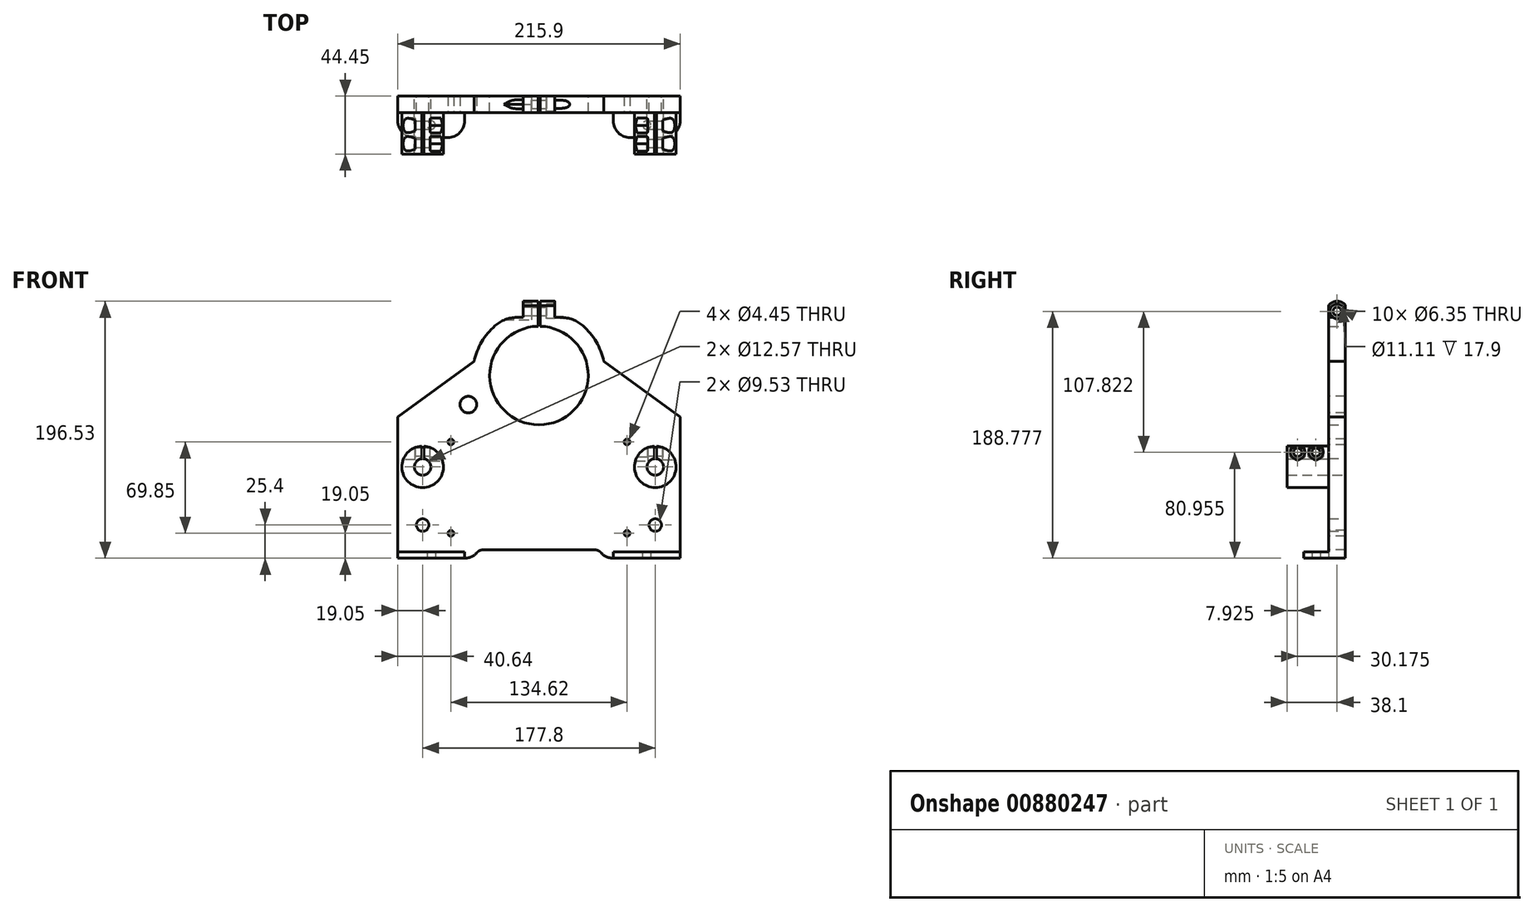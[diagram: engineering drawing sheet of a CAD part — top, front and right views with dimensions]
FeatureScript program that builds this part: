
annotation { "Feature Type Name" : "Feature", "Feature Type Description" : "" }
export const myFeature = defineFeature(function(context is Context, id is Id, definition is map)
    precondition{}
    {
        {
            var Q0;
            Q0=qCreatedBy(makeId("Front.planeOp"),FACE);
            var sketch = newSketch(context, id + "F0", { "sketchPlane" : qUnion([Q0])});
            skCircle(sketch, "E0", {"center": v(-88.9, 0) * mm, "radius": 6.29 * mm});
            skCircle(sketch, "E1", {"center": v(88.9, 0) * mm, "radius": 6.29 * mm});
            skCircle(sketch, "E2", {"center": v(-88.9, -44.45) * mm, "radius": 4.76 * mm});
            skCircle(sketch, "E3", {"center": v(88.9, -44.45) * mm, "radius": 4.76 * mm});
            skLineSegment(sketch, "E4.top", {"start": v(-107.95, -69.85) * mm, "end": v(107.95, -69.85) * mm});
            skLineSegment(sketch, "E4.left", {"start": v(-107.95, 38.1) * mm, "end": v(-107.95, -69.85) * mm});
            skLineSegment(sketch, "E4.right", {"start": v(107.95, 38.1) * mm, "end": v(107.95, -69.85) * mm});
            skPoint(sketch, "E4.middle", {"position": v(0, -15.87) * mm});
            skCircle(sketch, "E5", {"center": v(0, 69.85) * mm, "radius": 37.66 * mm});
            skArc(sketch, "E6", {"start": v(22.5, 100.6) * mm, "mid": v(0, 107.95) * mm, "end": v(-22.5, 100.6) * mm});
            skLineSegment(sketch, "E7", {"start": v(-107.95, 38.1) * mm, "end": v(-22.5, 100.6) * mm});
            skLineSegment(sketch, "E8", {"start": v(107.95, 38.1) * mm, "end": v(22.5, 100.6) * mm});
            skPoint(sketch, "E9.center.orphan", {"position": v(0, 0) * mm});
            skSolve(sketch);
        }
        {
            var Q0;
            Q0=qSketchRegion(id+"F0",true);
            extrude(context, id + "F1", {"entities" : qUnion([Q0]), "depth" : 12.7 * mm});
        }
        {
            var Q0;
            Q0=makeQuery(id+"F1.opExtrude","CAP_FACE",FACE,{"disambiguationData":[OSD([sQuery(id+"F0.wireOp",EDGE,"E9"),sQuery(id+"F0.wireOp",EDGE,"E0"),sQuery(id+"F0.wireOp",EDGE,"E1"),sQuery(id+"F0.wireOp",EDGE,"E2"),sQuery(id+"F0.wireOp",EDGE,"E3"),sQuery(id+"F0.wireOp",EDGE,"E4.bottom"),sQuery(id+"F0.wireOp",EDGE,"E4.top"),sQuery(id+"F0.wireOp",EDGE,"E4.left"),sQuery(id+"F0.wireOp",EDGE,"E4.right")])],"isStart":false});
            var sketch = newSketch(context, id + "F2", { "sketchPlane" : qUnion([Q0])});
            skCircle(sketch, "E10", {"center": v(0, -107.95) * mm, "radius": 63.5 * mm});
            skSolve(sketch);
        }
        {
            var Q0;
            Q0=qSketchRegion(id+"F2",true);
            extrude(context, id + "F3", {"entities" : qUnion([Q0]), "operationType" : NewBodyOperationType.REMOVE, "oppositeDirection" : true, "depth" : 25.4 * mm});
        }
        {
            var Q0;
            Q0=makeQuery(id+"F3.boolean.opBoolean","INTERSECT",EDGE,{"disambiguationData":[OD(0.0)],"derivedFrom":[makeQuery(id+"F1.opExtrude","SWEPT_FACE",FACE,{"disambiguationData":[OSD([sQuery(id+"F0.wireOp",EDGE,"E4.top")])]}),makeQuery(id+"F3.opExtrude","SWEPT_FACE",FACE,{"disambiguationData":[OSD([sQuery(id+"F2.wireOp",EDGE,"E10")])]})]});
            var Q1;
            Q1=makeQuery(id+"F3.boolean.opBoolean","INTERSECT",EDGE,{"disambiguationData":[OD(1.0)],"derivedFrom":[makeQuery(id+"F1.opExtrude","SWEPT_FACE",FACE,{"disambiguationData":[OSD([sQuery(id+"F0.wireOp",EDGE,"E4.top")])]}),makeQuery(id+"F3.opExtrude","SWEPT_FACE",FACE,{"disambiguationData":[OSD([sQuery(id+"F2.wireOp",EDGE,"E10")])]})]});
            fillet(context, id + "F4", {"entities" : qUnion([Q0, Q1]), "radius" : 12.7 * mm, "tangentPropagation" : true, "allowEdgeOverflow" : false});
        }
        {
            var Q0;
            Q0=makeQuery(id+"F1.opExtrude","CAP_FACE",FACE,{"disambiguationData":[OSD([sQuery(id+"F0.wireOp",EDGE,"E9"),sQuery(id+"F0.wireOp",EDGE,"E0"),sQuery(id+"F0.wireOp",EDGE,"E1"),sQuery(id+"F0.wireOp",EDGE,"E2"),sQuery(id+"F0.wireOp",EDGE,"E3"),sQuery(id+"F0.wireOp",EDGE,"E4.bottom"),sQuery(id+"F0.wireOp",EDGE,"E4.top"),sQuery(id+"F0.wireOp",EDGE,"E4.left"),sQuery(id+"F0.wireOp",EDGE,"E4.right")])],"isStart":false});
            var sketch = newSketch(context, id + "F5", { "sketchPlane" : qUnion([Q0])});
            skCircle(sketch, "E11.0", {"center": v(-88.9, 0) * mm, "radius": 6.29 * mm});
            skCircle(sketch, "E12", {"center": v(-88.9, 0) * mm, "radius": 15.88 * mm});
            skCircle(sketch, "E13.0", {"center": v(88.9, 0) * mm, "radius": 6.29 * mm});
            skCircle(sketch, "E14", {"center": v(88.9, 0) * mm, "radius": 15.88 * mm});
            skSolve(sketch);
        }
        {
            var Q0;
            Q0=qSketchRegion(id+"F5",true);
            extrude(context, id + "F6", {"entities" : qUnion([Q0]), "operationType" : NewBodyOperationType.ADD, "depth" : 31.75 * mm});
        }
        {
            var Q0;
            Q0=makeQuery(id+"F6.opExtrude","CAP_FACE",FACE,{"disambiguationData":[OSD([sQuery(id+"F5.wireOp",EDGE,"E11.0"),sQuery(id+"F5.wireOp",EDGE,"E12")])],"isStart":false});
            var sketch = newSketch(context, id + "F7", { "sketchPlane" : qUnion([Q0])});
            skLineSegment(sketch, "E15.bottom", {"start": v(-89.7, 1.72) * mm, "end": v(-88.1, 1.72) * mm});
            skLineSegment(sketch, "E15.top", {"start": v(-89.7, 19.66) * mm, "end": v(-88.1, 19.66) * mm});
            skLineSegment(sketch, "E15.left", {"start": v(-89.7, 1.72) * mm, "end": v(-89.7, 19.66) * mm});
            skLineSegment(sketch, "E15.right", {"start": v(-88.1, 1.72) * mm, "end": v(-88.1, 19.66) * mm});
            skLineSegment(sketch, "E16", {"start": v(-88.9, 1.72) * mm, "end": v(-88.9, 0) * mm});
            skPoint(sketch, "E16.endSnap0", {"position": v(-88.9, 1.72) * mm});
            skLineSegment(sketch, "E17.bottom", {"start": v(88.1, 20.83) * mm, "end": v(89.7, 20.83) * mm});
            skLineSegment(sketch, "E17.top", {"start": v(88.1, 3.08) * mm, "end": v(89.7, 3.08) * mm});
            skLineSegment(sketch, "E17.left", {"start": v(88.1, 20.83) * mm, "end": v(88.1, 3.08) * mm});
            skLineSegment(sketch, "E17.right", {"start": v(89.7, 20.83) * mm, "end": v(89.7, 3.08) * mm});
            skLineSegment(sketch, "E18", {"start": v(88.9, 0) * mm, "end": v(88.9, 3.08) * mm});
            skSolve(sketch);
        }
        {
            var Q0;
            Q0=qSketchRegion(id+"F7",true);
            var Q1;
            Q1=makeQuery(id+"F1.opExtrude","CAP_FACE",FACE,{"disambiguationData":[OSD([sQuery(id+"F0.wireOp",EDGE,"E9"),sQuery(id+"F0.wireOp",EDGE,"E0"),sQuery(id+"F0.wireOp",EDGE,"E1"),sQuery(id+"F0.wireOp",EDGE,"E2"),sQuery(id+"F0.wireOp",EDGE,"E3"),sQuery(id+"F0.wireOp",EDGE,"E4.bottom"),sQuery(id+"F0.wireOp",EDGE,"E4.top"),sQuery(id+"F0.wireOp",EDGE,"E4.left"),sQuery(id+"F0.wireOp",EDGE,"E4.right")])],"isStart":false});
            extrude(context, id + "F8", {"entities" : qUnion([Q0]), "operationType" : NewBodyOperationType.REMOVE, "endBound" : BoundingType.UP_TO_SURFACE, "oppositeDirection" : true, "endBoundEntityFace" : qUnion([Q1]), "depth" : 25.4 * mm});
        }
        {
            var Q0;
            Q0=makeQuery(id+"F1.opExtrude","SWEPT_FACE",FACE,{"disambiguationData":[OSD([sQuery(id+"F0.wireOp",EDGE,"E4.left")])]});
            var sketch = newSketch(context, id + "F9", { "sketchPlane" : qUnion([Q0])});
            skCircle(sketch, "E19", {"center": v(36.53, 11.1) * mm, "radius": 3.18 * mm});
            skCircle(sketch, "E20", {"center": v(22.56, 11.1) * mm, "radius": 3.18 * mm});
            skSolve(sketch);
        }
        {
            var Q0;
            Q0=qSketchRegion(id+"F9",true);
            extrude(context, id + "F10", {"entities" : qUnion([Q0]), "operationType" : NewBodyOperationType.REMOVE, "oppositeDirection" : true, "depth" : 224.54 * mm});
        }
        {
            var Q0;
            Q0=qCreatedBy(makeId("Right.planeOp"),FACE);
            var sketch = newSketch(context, id + "F11", { "sketchPlane" : qUnion([Q0])});
            skCircle(sketch, "E21.0", {"center": v(-36.53, 11.1) * mm, "radius": 3.17 * mm, "construction": true});
            skCircle(sketch, "E22.0", {"center": v(-22.56, 11.1) * mm, "radius": 3.18 * mm, "construction": true});
            skCircle(sketch, "E23.cCircle", {"center": v(-36.53, 11.1) * mm, "radius": 6.6 * mm, "construction": true});
            skLineSegment(sketch, "E23.0", {"start": v(-36.53, 17.7) * mm, "end": v(-30.8, 14.4) * mm});
            skLineSegment(sketch, "E23.1", {"start": v(-30.8, 14.4) * mm, "end": v(-30.8, 7.8) * mm});
            skLineSegment(sketch, "E23.2", {"start": v(-30.8, 7.8) * mm, "end": v(-36.53, 4.5) * mm});
            skLineSegment(sketch, "E23.3", {"start": v(-36.53, 4.5) * mm, "end": v(-42.24, 7.8) * mm});
            skLineSegment(sketch, "E23.4", {"start": v(-42.24, 7.8) * mm, "end": v(-42.24, 14.4) * mm});
            skLineSegment(sketch, "E23.5", {"start": v(-42.24, 14.4) * mm, "end": v(-36.53, 17.7) * mm});
            skCircle(sketch, "E24.cCircle", {"center": v(-22.56, 11.1) * mm, "radius": 6.6 * mm, "construction": true});
            skLineSegment(sketch, "E24.0", {"start": v(-28.27, 14.4) * mm, "end": v(-22.56, 17.7) * mm});
            skLineSegment(sketch, "E24.1", {"start": v(-22.56, 17.7) * mm, "end": v(-16.84, 14.4) * mm});
            skLineSegment(sketch, "E24.2", {"start": v(-16.84, 14.4) * mm, "end": v(-16.84, 7.8) * mm});
            skLineSegment(sketch, "E24.3", {"start": v(-16.84, 7.8) * mm, "end": v(-22.56, 4.5) * mm});
            skLineSegment(sketch, "E24.4", {"start": v(-22.56, 4.5) * mm, "end": v(-28.27, 7.8) * mm});
            skLineSegment(sketch, "E24.5", {"start": v(-28.27, 7.8) * mm, "end": v(-28.27, 14.4) * mm});
            skSolve(sketch);
        }
        {
            var Q0;
            Q0=makeQuery(id+"F11.imprint","IMPRINT",FACE,{"disambiguationData":[TD([[makeQuery(id+"F11.imprint","IMPRINT",EDGE,{"derivedFrom":sQuery(id+"F11.wireOp",EDGE,"E23.0")}),-1.0]])]});
            var Q1;
            Q1=makeQuery(id+"F11.imprint","IMPRINT",FACE,{"disambiguationData":[TD([[makeQuery(id+"F11.imprint","IMPRINT",EDGE,{"derivedFrom":sQuery(id+"F11.wireOp",EDGE,"E24.0")}),-1.0]])]});
            var Q2;
            Q2=sQuery(id+"F11.wireOp",EDGE,"E21.0");
            var Q3;
            Q3=sQuery(id+"F11.wireOp",EDGE,"E22.0");
            extrude(context, id + "F12", {"entities" : qUnion([Q0, Q1]), "operationType" : NewBodyOperationType.REMOVE, "surfaceEntities" : qUnion([Q2, Q3]), "oppositeDirection" : true, "depth" : 83.18 * mm, "hasSecondDirection" : true, "secondDirectionOppositeDirection" : false, "secondDirectionDepth" : 83.18 * mm});
        }
        {
            var Q0;
            Q0=makeQuery(id+"F1.opExtrude","SWEPT_FACE",FACE,{"disambiguationData":[OSD([sQuery(id+"F0.wireOp",EDGE,"E4.left")])]});
            var sketch = newSketch(context, id + "F13", { "sketchPlane" : qUnion([Q0])});
            skCircle(sketch, "E25.0", {"center": v(36.53, 11.1) * mm, "radius": 3.17 * mm, "construction": true});
            skCircle(sketch, "E26.0", {"center": v(22.56, 11.1) * mm, "radius": 3.18 * mm, "construction": true});
            skCircle(sketch, "E27", {"center": v(22.56, 11.1) * mm, "radius": 5.56 * mm});
            skCircle(sketch, "E28", {"center": v(36.53, 11.1) * mm, "radius": 5.56 * mm});
            skSolve(sketch);
        }
        {
            var Q0;
            Q0=qSketchRegion(id+"F13",true);
            extrude(context, id + "F14", {"entities" : qUnion([Q0]), "operationType" : NewBodyOperationType.REMOVE, "oppositeDirection" : true, "depth" : 13.33 * mm});
        }
        {
            var Q0;
            Q0=makeQuery(id+"F1.opExtrude","SWEPT_FACE",FACE,{"disambiguationData":[OSD([sQuery(id+"F0.wireOp",EDGE,"E4.right")])]});
            var sketch = newSketch(context, id + "F15", { "sketchPlane" : qUnion([Q0])});
            skCircle(sketch, "E29.0", {"center": v(-36.53, 11.1) * mm, "radius": 3.17 * mm, "construction": true});
            skCircle(sketch, "E29.1", {"center": v(-22.56, 11.1) * mm, "radius": 3.18 * mm, "construction": true});
            skCircle(sketch, "E30", {"center": v(-36.53, 11.1) * mm, "radius": 5.56 * mm});
            skCircle(sketch, "E31", {"center": v(-22.56, 11.1) * mm, "radius": 5.56 * mm});
            skSolve(sketch);
        }
        {
            var Q0;
            Q0=qSketchRegion(id+"F15",true);
            extrude(context, id + "F16", {"entities" : qUnion([Q0]), "operationType" : NewBodyOperationType.REMOVE, "oppositeDirection" : true, "depth" : 13.33 * mm});
        }
        {
            var Q0;
            {var subQ1=sQuery(id+"F0.wireOp",EDGE,"E4.left");var subQ2=sQuery(id+"F0.wireOp",EDGE,"E4.top");Q0=makeQuery(id+"F3.boolean.opBoolean","SPLIT",FACE,{"disambiguationData":[TD([makeQuery(id+"F1.opExtrude","SWEPT_FACE",FACE,{"disambiguationData":[OSD([subQ1])]})])],"derivedFrom":makeQuery(id+"F1.opExtrude","SWEPT_FACE",FACE,{"disambiguationData":[OSD([subQ2])]})});}
            var sketch = newSketch(context, id + "F17", { "sketchPlane" : qUnion([Q0])});
            skLineSegment(sketch, "E32.0", {"start": v(56.8, 12.7) * mm, "end": v(107.95, 12.7) * mm});
            skLineSegment(sketch, "E33", {"start": v(107.95, 12.7) * mm, "end": v(107.95, 31.75) * mm});
            skLineSegment(sketch, "E34", {"start": v(107.95, 31.75) * mm, "end": v(56.8, 31.75) * mm});
            skLineSegment(sketch, "E35", {"start": v(56.8, 31.75) * mm, "end": v(56.8, 12.7) * mm});
            skCircle(sketch, "E36", {"center": v(82.37, 22.23) * mm, "radius": 3.18 * mm});
            skLineSegment(sketch, "E37", {"start": v(107.95, 22.23) * mm, "end": v(56.8, 22.23) * mm, "construction": true});
            skLineSegment(sketch, "E38.bottom", {"start": v(-107.95, 12.7) * mm, "end": v(-56.8, 12.7) * mm});
            skLineSegment(sketch, "E38.top", {"start": v(-107.95, 31.75) * mm, "end": v(-56.8, 31.75) * mm});
            skLineSegment(sketch, "E38.left", {"start": v(-107.95, 12.7) * mm, "end": v(-107.95, 31.75) * mm});
            skLineSegment(sketch, "E38.right", {"start": v(-56.8, 12.7) * mm, "end": v(-56.8, 31.75) * mm});
            skCircle(sketch, "E39", {"center": v(-82.37, 22.22) * mm, "radius": 3.18 * mm});
            skPoint(sketch, "E39.centerSnap0", {"position": v(-82.37, 31.75) * mm});
            skSolve(sketch);
        }
        {
            var Q0;
            Q0=qSketchRegion(id+"F17",true);
            extrude(context, id + "F18", {"entities" : qUnion([Q0]), "operationType" : NewBodyOperationType.ADD, "oppositeDirection" : true, "depth" : 4.75 * mm});
        }
        {
            var Q0;
            Q0=makeQuery(id+"F18.opExtrude","SWEPT_EDGE",EDGE,{"disambiguationData":[OSD([sQuery(id+"F17.wireOp",EDGE,"E34"),sQuery(id+"F17.wireOp",EDGE,"E35")])]});
            var Q1;
            Q1=makeQuery(id+"F18.opExtrude","SWEPT_EDGE",EDGE,{"disambiguationData":[OSD([sQuery(id+"F17.wireOp",EDGE,"E33"),sQuery(id+"F17.wireOp",EDGE,"E34")])]});
            var Q2;
            Q2=makeQuery(id+"F18.opExtrude","SWEPT_EDGE",EDGE,{"disambiguationData":[OSD([sQuery(id+"F17.wireOp",EDGE,"E38.top"),sQuery(id+"F17.wireOp",EDGE,"E38.right")])]});
            var Q3;
            Q3=makeQuery(id+"F18.opExtrude","SWEPT_EDGE",EDGE,{"disambiguationData":[OSD([sQuery(id+"F17.wireOp",EDGE,"E38.top"),sQuery(id+"F17.wireOp",EDGE,"E38.left")])]});
            fillet(context, id + "F19", {"entities" : qUnion([Q0, Q1, Q2, Q3]), "radius" : 12.7 * mm, "tangentPropagation" : true, "allowEdgeOverflow" : false});
        }
        {
            var Q0;
            {var subQ0=sQuery(id+"F0.wireOp",EDGE,"E8");var subQ1=sQuery(id+"F0.wireOp",EDGE,"E7");var subQ2=sQuery(id+"F0.wireOp",EDGE,"E6");var subQ3=sQuery(id+"F0.wireOp",EDGE,"E5");var subQ4=sQuery(id+"F0.wireOp",EDGE,"E4.right");var subQ5=sQuery(id+"F0.wireOp",EDGE,"E4.left");var subQ6=sQuery(id+"F0.wireOp",EDGE,"E4.top");var subQ7=sQuery(id+"F0.wireOp",EDGE,"E3");var subQ8=sQuery(id+"F0.wireOp",EDGE,"E2");var subQ9=sQuery(id+"F0.wireOp",EDGE,"E1");var subQ10=sQuery(id+"F0.wireOp",EDGE,"E0");var subQ11=sQuery(id+"F7.wireOp",EDGE,"E15.bottom");Q0=makeQuery(id+"F8.boolean.opBoolean","MERGE",FACE,{"derivedFrom":[makeQuery(id+"F1.opExtrude","CAP_FACE",FACE,{"disambiguationData":[OSD([subQ10,subQ9,subQ8,subQ7,subQ6,subQ5,subQ4,subQ3,subQ2,subQ1,subQ0])],"isStart":false}),makeQuery(id+"F8.opExtrude","CAP_FACE",FACE,{"disambiguationData":[OSD([subQ10,subQ9,subQ8,subQ7,subQ6,subQ5,subQ4,subQ3,subQ2,subQ1,subQ0]),ownerDisambiguation([makeQuery(id+"F7.imprint","IMPRINT",EDGE,{"disambiguationData":[TD([[makeQuery(id+"F7.imprint","IMPRINT",VERTEX,{"derivedFrom":subQ11}),1.0]])],"derivedFrom":subQ11})])],"isStart":false}),makeQuery(id+"F8.opExtrude","CAP_FACE",FACE,{"disambiguationData":[OSD([subQ10,subQ9,subQ8,subQ7,subQ6,subQ5,subQ4,subQ3,subQ2,subQ1,subQ0]),ownerDisambiguation([makeQuery(id+"F7.imprint","IMPRINT",EDGE,{"derivedFrom":sQuery(id+"F7.wireOp",EDGE,"E17.bottom")})])],"isStart":false})]});}
            var sketch = newSketch(context, id + "F20", { "sketchPlane" : qUnion([Q0])});
            skCircle(sketch, "E40", {"center": v(0, 69.85) * mm, "radius": 50.8 * mm});
            skCircle(sketch, "E41.0", {"center": v(0, 69.85) * mm, "radius": 37.66 * mm});
            skSolve(sketch);
        }
        {
            var Q0;
            Q0=qSketchRegion(id+"F20",true);
            extrude(context, id + "F21", {"entities" : qUnion([Q0]), "operationType" : NewBodyOperationType.ADD, "oppositeDirection" : true, "depth" : 12.7 * mm});
        }
        {
            var Q0;
            {var subQ0=sQuery(id+"F0.wireOp",EDGE,"E8");var subQ1=sQuery(id+"F0.wireOp",EDGE,"E7");var subQ2=sQuery(id+"F0.wireOp",EDGE,"E6");var subQ3=sQuery(id+"F0.wireOp",EDGE,"E5");var subQ4=sQuery(id+"F0.wireOp",EDGE,"E4.right");var subQ5=sQuery(id+"F0.wireOp",EDGE,"E4.left");var subQ6=sQuery(id+"F0.wireOp",EDGE,"E4.top");var subQ7=sQuery(id+"F0.wireOp",EDGE,"E3");var subQ8=sQuery(id+"F0.wireOp",EDGE,"E2");var subQ9=sQuery(id+"F0.wireOp",EDGE,"E1");var subQ10=sQuery(id+"F0.wireOp",EDGE,"E0");var subQ11=sQuery(id+"F7.wireOp",EDGE,"E15.bottom");Q0=makeQuery(id+"F21.boolean.opBoolean","MERGE",FACE,{"derivedFrom":[makeQuery(id+"F8.boolean.opBoolean","MERGE",FACE,{"derivedFrom":[makeQuery(id+"F1.opExtrude","CAP_FACE",FACE,{"disambiguationData":[OSD([subQ10,subQ9,subQ8,subQ7,subQ6,subQ5,subQ4,subQ3,subQ2,subQ1,subQ0])],"isStart":false}),makeQuery(id+"F8.opExtrude","CAP_FACE",FACE,{"disambiguationData":[OSD([subQ10,subQ9,subQ8,subQ7,subQ6,subQ5,subQ4,subQ3,subQ2,subQ1,subQ0]),ownerDisambiguation([makeQuery(id+"F7.imprint","IMPRINT",EDGE,{"disambiguationData":[TD([[makeQuery(id+"F7.imprint","IMPRINT",VERTEX,{"derivedFrom":subQ11}),1.0]])],"derivedFrom":subQ11})])],"isStart":false}),makeQuery(id+"F8.opExtrude","CAP_FACE",FACE,{"disambiguationData":[OSD([subQ10,subQ9,subQ8,subQ7,subQ6,subQ5,subQ4,subQ3,subQ2,subQ1,subQ0]),ownerDisambiguation([makeQuery(id+"F7.imprint","IMPRINT",EDGE,{"derivedFrom":sQuery(id+"F7.wireOp",EDGE,"E17.bottom")})])],"isStart":false})]}),makeQuery(id+"F21.opExtrude","CAP_FACE",FACE,{"disambiguationData":[OSD([sQuery(id+"F20.wireOp",EDGE,"E40"),sQuery(id+"F20.wireOp",EDGE,"E41.0")])],"isStart":true})]});}
            var sketch = newSketch(context, id + "F22", { "sketchPlane" : qUnion([Q0])});
            skLineSegment(sketch, "E42.bottom", {"start": v(-0.8, 123.3) * mm, "end": v(0.8, 123.3) * mm});
            skLineSegment(sketch, "E42.top", {"start": v(-0.8, 97.65) * mm, "end": v(0.8, 97.65) * mm});
            skLineSegment(sketch, "E42.left", {"start": v(-0.8, 123.3) * mm, "end": v(-0.8, 97.65) * mm});
            skLineSegment(sketch, "E42.right", {"start": v(0.8, 123.3) * mm, "end": v(0.8, 97.65) * mm});
            skLineSegment(sketch, "E43", {"start": v(0, 69.85) * mm, "end": v(0, 97.65) * mm, "construction": true});
            skSolve(sketch);
        }
        {
            var Q0;
            Q0=qSketchRegion(id+"F22",true);
            extrude(context, id + "F23", {"entities" : qUnion([Q0]), "operationType" : NewBodyOperationType.REMOVE, "oppositeDirection" : true, "depth" : 25.4 * mm});
        }
        {
            var Q0;
            {var subQ0=sQuery(id+"F0.wireOp",EDGE,"E8");var subQ1=sQuery(id+"F0.wireOp",EDGE,"E7");var subQ2=sQuery(id+"F0.wireOp",EDGE,"E6");var subQ3=sQuery(id+"F0.wireOp",EDGE,"E5");var subQ4=sQuery(id+"F0.wireOp",EDGE,"E4.right");var subQ5=sQuery(id+"F0.wireOp",EDGE,"E4.left");var subQ6=sQuery(id+"F0.wireOp",EDGE,"E4.top");var subQ7=sQuery(id+"F0.wireOp",EDGE,"E3");var subQ8=sQuery(id+"F0.wireOp",EDGE,"E2");var subQ9=sQuery(id+"F0.wireOp",EDGE,"E1");var subQ10=sQuery(id+"F0.wireOp",EDGE,"E0");var subQ11=sQuery(id+"F7.wireOp",EDGE,"E15.bottom");Q0=makeQuery(id+"F21.boolean.opBoolean","MERGE",FACE,{"derivedFrom":[makeQuery(id+"F8.boolean.opBoolean","MERGE",FACE,{"derivedFrom":[makeQuery(id+"F1.opExtrude","CAP_FACE",FACE,{"disambiguationData":[OSD([subQ10,subQ9,subQ8,subQ7,subQ6,subQ5,subQ4,subQ3,subQ2,subQ1,subQ0])],"isStart":false}),makeQuery(id+"F8.opExtrude","CAP_FACE",FACE,{"disambiguationData":[OSD([subQ10,subQ9,subQ8,subQ7,subQ6,subQ5,subQ4,subQ3,subQ2,subQ1,subQ0]),ownerDisambiguation([makeQuery(id+"F7.imprint","IMPRINT",EDGE,{"disambiguationData":[TD([[makeQuery(id+"F7.imprint","IMPRINT",VERTEX,{"derivedFrom":subQ11}),1.0]])],"derivedFrom":subQ11})])],"isStart":false}),makeQuery(id+"F8.opExtrude","CAP_FACE",FACE,{"disambiguationData":[OSD([subQ10,subQ9,subQ8,subQ7,subQ6,subQ5,subQ4,subQ3,subQ2,subQ1,subQ0]),ownerDisambiguation([makeQuery(id+"F7.imprint","IMPRINT",EDGE,{"derivedFrom":sQuery(id+"F7.wireOp",EDGE,"E17.bottom")})])],"isStart":false})]}),makeQuery(id+"F21.opExtrude","CAP_FACE",FACE,{"disambiguationData":[OSD([sQuery(id+"F20.wireOp",EDGE,"E40"),sQuery(id+"F20.wireOp",EDGE,"E41.0")])],"isStart":true})]});}
            var sketch = newSketch(context, id + "F24", { "sketchPlane" : qUnion([Q0])});
            skLineSegment(sketch, "E44.bottom", {"start": v(-6.99, 124.23) * mm, "end": v(-32.38, 124.23) * mm});
            skLineSegment(sketch, "E44.top", {"start": v(-6.98, 114.3) * mm, "end": v(-32.39, 114.3) * mm});
            skLineSegment(sketch, "E44.left", {"start": v(-6.99, 124.23) * mm, "end": v(-6.98, 114.3) * mm});
            skLineSegment(sketch, "E44.right", {"start": v(-32.39, 124.23) * mm, "end": v(-32.39, 114.3) * mm});
            skLineSegment(sketch, "E45.bottom", {"start": v(6.99, 124.23) * mm, "end": v(32.39, 124.23) * mm});
            skLineSegment(sketch, "E45.top", {"start": v(6.98, 114.3) * mm, "end": v(32.38, 114.3) * mm});
            skLineSegment(sketch, "E45.left", {"start": v(6.99, 124.23) * mm, "end": v(6.98, 114.3) * mm});
            skLineSegment(sketch, "E45.right", {"start": v(32.39, 124.23) * mm, "end": v(32.39, 114.3) * mm});
            skLineSegment(sketch, "E46", {"start": v(-6.99, 114.3) * mm, "end": v(6.98, 114.3) * mm, "construction": true});
            skLineSegment(sketch, "E47", {"start": v(0, 69.85) * mm, "end": v(0, 114.3) * mm, "construction": true});
            skSolve(sketch);
        }
        {
            var Q0;
            Q0=qSketchRegion(id+"F24",true);
            extrude(context, id + "F25", {"entities" : qUnion([Q0]), "operationType" : NewBodyOperationType.REMOVE, "oppositeDirection" : true, "depth" : 25.4 * mm});
        }
        {
            var Q0;
            {var subQ0=sQuery(id+"F0.wireOp",EDGE,"E8");var subQ1=sQuery(id+"F0.wireOp",EDGE,"E7");var subQ2=sQuery(id+"F0.wireOp",EDGE,"E6");var subQ3=sQuery(id+"F0.wireOp",EDGE,"E5");var subQ4=sQuery(id+"F0.wireOp",EDGE,"E4.right");var subQ5=sQuery(id+"F0.wireOp",EDGE,"E4.left");var subQ6=sQuery(id+"F0.wireOp",EDGE,"E4.top");var subQ7=sQuery(id+"F0.wireOp",EDGE,"E3");var subQ8=sQuery(id+"F0.wireOp",EDGE,"E2");var subQ9=sQuery(id+"F0.wireOp",EDGE,"E1");var subQ10=sQuery(id+"F0.wireOp",EDGE,"E0");var subQ11=sQuery(id+"F7.wireOp",EDGE,"E15.bottom");Q0=makeQuery(id+"F21.boolean.opBoolean","MERGE",FACE,{"derivedFrom":[makeQuery(id+"F8.boolean.opBoolean","MERGE",FACE,{"derivedFrom":[makeQuery(id+"F1.opExtrude","CAP_FACE",FACE,{"disambiguationData":[OSD([subQ10,subQ9,subQ8,subQ7,subQ6,subQ5,subQ4,subQ3,subQ2,subQ1,subQ0])],"isStart":false}),makeQuery(id+"F8.opExtrude","CAP_FACE",FACE,{"disambiguationData":[OSD([subQ10,subQ9,subQ8,subQ7,subQ6,subQ5,subQ4,subQ3,subQ2,subQ1,subQ0]),ownerDisambiguation([makeQuery(id+"F7.imprint","IMPRINT",EDGE,{"disambiguationData":[TD([[makeQuery(id+"F7.imprint","IMPRINT",VERTEX,{"derivedFrom":subQ11}),1.0]])],"derivedFrom":subQ11})])],"isStart":false}),makeQuery(id+"F8.opExtrude","CAP_FACE",FACE,{"disambiguationData":[OSD([subQ10,subQ9,subQ8,subQ7,subQ6,subQ5,subQ4,subQ3,subQ2,subQ1,subQ0]),ownerDisambiguation([makeQuery(id+"F7.imprint","IMPRINT",EDGE,{"derivedFrom":sQuery(id+"F7.wireOp",EDGE,"E17.bottom")})])],"isStart":false})]}),makeQuery(id+"F21.opExtrude","CAP_FACE",FACE,{"disambiguationData":[OSD([sQuery(id+"F20.wireOp",EDGE,"E40"),sQuery(id+"F20.wireOp",EDGE,"E41.0")])],"isStart":true})]});}
            var sketch = newSketch(context, id + "F26", { "sketchPlane" : qUnion([Q0])});
            skLineSegment(sketch, "E48.bottom", {"start": v(-0.8, 107.5) * mm, "end": v(-6.99, 107.5) * mm});
            skLineSegment(sketch, "E48.top", {"start": v(-0.8, 123.37) * mm, "end": v(-6.99, 123.37) * mm});
            skLineSegment(sketch, "E48.left", {"start": v(-0.8, 107.5) * mm, "end": v(-0.8, 123.37) * mm});
            skLineSegment(sketch, "E48.right", {"start": v(-6.99, 107.5) * mm, "end": v(-6.99, 123.37) * mm});
            skLineSegment(sketch, "E49.bottom", {"start": v(0.8, 107.5) * mm, "end": v(6.99, 107.5) * mm});
            skLineSegment(sketch, "E49.top", {"start": v(0.8, 123.37) * mm, "end": v(6.99, 123.37) * mm});
            skLineSegment(sketch, "E49.left", {"start": v(0.8, 107.5) * mm, "end": v(0.8, 123.37) * mm});
            skLineSegment(sketch, "E49.right", {"start": v(6.99, 107.5) * mm, "end": v(6.99, 123.37) * mm});
            skSolve(sketch);
        }
        {
            var Q0;
            Q0=qSketchRegion(id+"F26",true);
            extrude(context, id + "F27", {"entities" : qUnion([Q0]), "operationType" : NewBodyOperationType.ADD, "oppositeDirection" : true, "depth" : 12.7 * mm});
        }
        {
            var Q0;
            Q0=makeQuery(id+"F23.boolean.opBoolean","COPY",FACE,{"derivedFrom":makeQuery(id+"F23.opExtrude","SWEPT_FACE",FACE,{"disambiguationData":[OSD([sQuery(id+"F22.wireOp",EDGE,"E42.left")])]})});
            var sketch = newSketch(context, id + "F28", { "sketchPlane" : qUnion([Q0])});
            skCircle(sketch, "E50", {"center": v(-6.35, 118.93) * mm, "radius": 3.18 * mm});
            skLineSegment(sketch, "E51", {"start": v(-6.35, 118.93) * mm, "end": v(-6.35, 107.5) * mm});
            skSolve(sketch);
        }
        {
            var Q0;
            Q0=qSketchRegion(id+"F28",true);
            extrude(context, id + "F29", {"entities" : qUnion([Q0]), "operationType" : NewBodyOperationType.REMOVE, "oppositeDirection" : true, "depth" : 25.4 * mm, "hasSecondDirection" : true, "secondDirectionOppositeDirection" : false, "secondDirectionDepth" : 25.4 * mm});
        }
        {
            var Q0;
            Q0=makeQuery(id+"F27.boolean.opBoolean","MERGE",FACE,{"derivedFrom":[makeQuery(id+"F25.boolean.opBoolean","COPY",FACE,{"derivedFrom":makeQuery(id+"F25.opExtrude","SWEPT_FACE",FACE,{"disambiguationData":[OSD([sQuery(id+"F24.wireOp",EDGE,"E45.left")])]})}),makeQuery(id+"F27.opExtrude","SWEPT_FACE",FACE,{"disambiguationData":[OSD([sQuery(id+"F26.wireOp",EDGE,"E49.right")])]})]});
            var sketch = newSketch(context, id + "F30", { "sketchPlane" : qUnion([Q0])});
            skArc(sketch, "E52", {"start": v(0, 123.37) * mm, "mid": v(-6.35, 126.68) * mm, "end": v(-12.7, 123.37) * mm});
            skLineSegment(sketch, "E53.0", {"start": v(0, 123.37) * mm, "end": v(-12.7, 123.37) * mm});
            skSolve(sketch);
        }
        {
            var Q0;
            Q0=qSketchRegion(id+"F30",true);
            var Q1;
            Q1=makeQuery(id+"F27.boolean.opBoolean","MERGE",FACE,{"derivedFrom":[makeQuery(id+"F23.boolean.opBoolean","COPY",FACE,{"derivedFrom":makeQuery(id+"F23.opExtrude","SWEPT_FACE",FACE,{"disambiguationData":[OSD([sQuery(id+"F22.wireOp",EDGE,"E42.right")])]})}),makeQuery(id+"F27.opExtrude","SWEPT_FACE",FACE,{"disambiguationData":[OSD([sQuery(id+"F26.wireOp",EDGE,"E49.left")])]})]});
            extrude(context, id + "F31", {"entities" : qUnion([Q0]), "operationType" : NewBodyOperationType.ADD, "endBound" : BoundingType.UP_TO_SURFACE, "oppositeDirection" : true, "endBoundEntityFace" : qUnion([Q1]), "depth" : 25.4 * mm});
        }
        {
            var Q0;
            Q0=makeQuery(id+"F27.boolean.opBoolean","MERGE",FACE,{"derivedFrom":[makeQuery(id+"F25.boolean.opBoolean","COPY",FACE,{"derivedFrom":makeQuery(id+"F25.opExtrude","SWEPT_FACE",FACE,{"disambiguationData":[OSD([sQuery(id+"F24.wireOp",EDGE,"E44.left")])]})}),makeQuery(id+"F27.opExtrude","SWEPT_FACE",FACE,{"disambiguationData":[OSD([sQuery(id+"F26.wireOp",EDGE,"E48.right")])]})]});
            var sketch = newSketch(context, id + "F32", { "sketchPlane" : qUnion([Q0])});
            skArc(sketch, "E54", {"start": v(12.7, 123.37) * mm, "mid": v(6.35, 126.68) * mm, "end": v(0, 123.37) * mm});
            skLineSegment(sketch, "E55.0", {"start": v(0, 123.37) * mm, "end": v(12.7, 123.37) * mm});
            skSolve(sketch);
        }
        {
            var Q0;
            Q0=qSketchRegion(id+"F32",true);
            var Q1;
            Q1=makeQuery(id+"F27.boolean.opBoolean","MERGE",FACE,{"derivedFrom":[makeQuery(id+"F23.boolean.opBoolean","COPY",FACE,{"derivedFrom":makeQuery(id+"F23.opExtrude","SWEPT_FACE",FACE,{"disambiguationData":[OSD([sQuery(id+"F22.wireOp",EDGE,"E42.left")])]})}),makeQuery(id+"F27.opExtrude","SWEPT_FACE",FACE,{"disambiguationData":[OSD([sQuery(id+"F26.wireOp",EDGE,"E48.left")])]})]});
            extrude(context, id + "F33", {"entities" : qUnion([Q0]), "operationType" : NewBodyOperationType.ADD, "endBound" : BoundingType.UP_TO_SURFACE, "oppositeDirection" : true, "endBoundEntityFace" : qUnion([Q1]), "depth" : 25.4 * mm});
        }
        {
            var Q0;
            {var subQ2=sQuery(id+"F0.wireOp",EDGE,"E7");var subQ13=sQuery(id+"F20.wireOp",EDGE,"E40");Q0=makeQuery(id+"F25.boolean.opBoolean","INTERSECT",EDGE,{"derivedFrom":[makeQuery(id+"F23.boolean.opBoolean","SPLIT",FACE,{"disambiguationData":[TD([makeQuery(id+"F1.opExtrude","SWEPT_FACE",FACE,{"disambiguationData":[OSD([subQ2])]})])],"derivedFrom":makeQuery(id+"F21.opExtrude","SWEPT_FACE",FACE,{"disambiguationData":[OSD([subQ13])]})}),makeQuery(id+"F25.opExtrude","SWEPT_FACE",FACE,{"disambiguationData":[OSD([sQuery(id+"F24.wireOp",EDGE,"E44.top")])]})]});}
            var Q1;
            {var subQ1=sQuery(id+"F0.wireOp",EDGE,"E8");var subQ13=sQuery(id+"F20.wireOp",EDGE,"E40");Q1=makeQuery(id+"F25.boolean.opBoolean","INTERSECT",EDGE,{"derivedFrom":[makeQuery(id+"F23.boolean.opBoolean","SPLIT",FACE,{"disambiguationData":[TD([makeQuery(id+"F1.opExtrude","SWEPT_FACE",FACE,{"disambiguationData":[OSD([subQ1])]})])],"derivedFrom":makeQuery(id+"F21.opExtrude","SWEPT_FACE",FACE,{"disambiguationData":[OSD([subQ13])]})}),makeQuery(id+"F25.opExtrude","SWEPT_FACE",FACE,{"disambiguationData":[OSD([sQuery(id+"F24.wireOp",EDGE,"E45.top")])]})]});}
            fillet(context, id + "F34", {"entities" : qUnion([Q0, Q1]), "radius" : 25.4 * mm, "tangentPropagation" : true, "allowEdgeOverflow" : false});
        }
        {
            var Q0;
            Q0=makeQuery(id+"F31.boolean.opBoolean","MERGE",FACE,{"derivedFrom":[makeQuery(id+"F27.boolean.opBoolean","MERGE",FACE,{"derivedFrom":[makeQuery(id+"F25.boolean.opBoolean","COPY",FACE,{"derivedFrom":makeQuery(id+"F25.opExtrude","SWEPT_FACE",FACE,{"disambiguationData":[OSD([sQuery(id+"F24.wireOp",EDGE,"E45.left")])]})}),makeQuery(id+"F27.opExtrude","SWEPT_FACE",FACE,{"disambiguationData":[OSD([sQuery(id+"F26.wireOp",EDGE,"E49.right")])]})]}),makeQuery(id+"F31.opExtrude","CAP_FACE",FACE,{"disambiguationData":[OSD([sQuery(id+"F30.wireOp",EDGE,"E52"),sQuery(id+"F30.wireOp",EDGE,"E53.0")])],"isStart":true})]});
            var sketch = newSketch(context, id + "F35", { "sketchPlane" : qUnion([Q0])});
            skCircle(sketch, "E56", {"center": v(-6.35, 118.93) * mm, "radius": 5.56 * mm});
            skSolve(sketch);
        }
        {
            var Q0;
            Q0=qSketchRegion(id+"F35",true);
            extrude(context, id + "F36", {"entities" : qUnion([Q0]), "operationType" : NewBodyOperationType.REMOVE, "depth" : 28.93 * mm});
        }
        {
            var Q0;
            Q0=makeQuery(id+"F33.boolean.opBoolean","MERGE",FACE,{"derivedFrom":[makeQuery(id+"F27.boolean.opBoolean","MERGE",FACE,{"derivedFrom":[makeQuery(id+"F25.boolean.opBoolean","COPY",FACE,{"derivedFrom":makeQuery(id+"F25.opExtrude","SWEPT_FACE",FACE,{"disambiguationData":[OSD([sQuery(id+"F24.wireOp",EDGE,"E44.left")])]})}),makeQuery(id+"F27.opExtrude","SWEPT_FACE",FACE,{"disambiguationData":[OSD([sQuery(id+"F26.wireOp",EDGE,"E48.right")])]})]}),makeQuery(id+"F33.opExtrude","CAP_FACE",FACE,{"disambiguationData":[OSD([sQuery(id+"F32.wireOp",EDGE,"E54"),sQuery(id+"F32.wireOp",EDGE,"E55.0")])],"isStart":true})]});
            var sketch = newSketch(context, id + "F37", { "sketchPlane" : qUnion([Q0])});
            skCircle(sketch, "E57.cCircle", {"center": v(6.35, 118.93) * mm, "radius": 6.6 * mm, "construction": true});
            skLineSegment(sketch, "E57.0", {"start": v(0.63, 122.23) * mm, "end": v(6.35, 125.53) * mm});
            skLineSegment(sketch, "E57.1", {"start": v(6.35, 125.53) * mm, "end": v(12.07, 122.23) * mm});
            skLineSegment(sketch, "E57.2", {"start": v(12.07, 122.23) * mm, "end": v(12.07, 115.63) * mm});
            skLineSegment(sketch, "E57.3", {"start": v(12.07, 115.63) * mm, "end": v(6.35, 112.32) * mm});
            skLineSegment(sketch, "E57.4", {"start": v(6.35, 112.32) * mm, "end": v(0.63, 115.63) * mm});
            skLineSegment(sketch, "E57.5", {"start": v(0.63, 115.63) * mm, "end": v(0.63, 122.23) * mm});
            skSolve(sketch);
        }
        {
            var Q0;
            Q0=qSketchRegion(id+"F37",true);
            extrude(context, id + "F38", {"entities" : qUnion([Q0]), "operationType" : NewBodyOperationType.REMOVE, "depth" : 22.22 * mm});
        }
        {
            var Q0;
            {var subQ0=sQuery(id+"F0.wireOp",EDGE,"E8");var subQ1=sQuery(id+"F0.wireOp",EDGE,"E7");var subQ2=sQuery(id+"F0.wireOp",EDGE,"E6");var subQ3=sQuery(id+"F0.wireOp",EDGE,"E5");var subQ4=sQuery(id+"F0.wireOp",EDGE,"E4.right");var subQ5=sQuery(id+"F0.wireOp",EDGE,"E4.left");var subQ6=sQuery(id+"F0.wireOp",EDGE,"E4.top");var subQ7=sQuery(id+"F0.wireOp",EDGE,"E3");var subQ8=sQuery(id+"F0.wireOp",EDGE,"E2");var subQ9=sQuery(id+"F0.wireOp",EDGE,"E1");var subQ10=sQuery(id+"F0.wireOp",EDGE,"E0");var subQ11=sQuery(id+"F7.wireOp",EDGE,"E15.bottom");Q0=makeQuery(id+"F27.boolean.opBoolean","MERGE",FACE,{"derivedFrom":[makeQuery(id+"F21.boolean.opBoolean","MERGE",FACE,{"derivedFrom":[makeQuery(id+"F8.boolean.opBoolean","MERGE",FACE,{"derivedFrom":[makeQuery(id+"F1.opExtrude","CAP_FACE",FACE,{"disambiguationData":[OSD([subQ10,subQ9,subQ8,subQ7,subQ6,subQ5,subQ4,subQ3,subQ2,subQ1,subQ0])],"isStart":false}),makeQuery(id+"F8.opExtrude","CAP_FACE",FACE,{"disambiguationData":[OSD([subQ10,subQ9,subQ8,subQ7,subQ6,subQ5,subQ4,subQ3,subQ2,subQ1,subQ0]),ownerDisambiguation([makeQuery(id+"F7.imprint","IMPRINT",EDGE,{"disambiguationData":[TD([[makeQuery(id+"F7.imprint","IMPRINT",VERTEX,{"derivedFrom":subQ11}),1.0]])],"derivedFrom":subQ11})])],"isStart":false}),makeQuery(id+"F8.opExtrude","CAP_FACE",FACE,{"disambiguationData":[OSD([subQ10,subQ9,subQ8,subQ7,subQ6,subQ5,subQ4,subQ3,subQ2,subQ1,subQ0]),ownerDisambiguation([makeQuery(id+"F7.imprint","IMPRINT",EDGE,{"derivedFrom":sQuery(id+"F7.wireOp",EDGE,"E17.bottom")})])],"isStart":false})]}),makeQuery(id+"F21.opExtrude","CAP_FACE",FACE,{"disambiguationData":[OSD([sQuery(id+"F20.wireOp",EDGE,"E40"),sQuery(id+"F20.wireOp",EDGE,"E41.0")])],"isStart":true})]}),makeQuery(id+"F27.opExtrude","CAP_FACE",FACE,{"disambiguationData":[OSD([sQuery(id+"F26.wireOp",EDGE,"E48.bottom"),sQuery(id+"F26.wireOp",EDGE,"E48.top"),sQuery(id+"F26.wireOp",EDGE,"E48.left"),sQuery(id+"F26.wireOp",EDGE,"E48.right")])],"isStart":true}),makeQuery(id+"F27.opExtrude","CAP_FACE",FACE,{"disambiguationData":[OSD([sQuery(id+"F26.wireOp",EDGE,"E49.bottom"),sQuery(id+"F26.wireOp",EDGE,"E49.top"),sQuery(id+"F26.wireOp",EDGE,"E49.left"),sQuery(id+"F26.wireOp",EDGE,"E49.right")])],"isStart":true})]});}
            var sketch = newSketch(context, id + "F39", { "sketchPlane" : qUnion([Q0])});
            skLineSegment(sketch, "E58.bottom", {"start": v(-67.31, 19.05) * mm, "end": v(67.31, 19.05) * mm, "construction": true});
            skLineSegment(sketch, "E58.top", {"start": v(-67.31, -50.8) * mm, "end": v(67.31, -50.8) * mm, "construction": true});
            skLineSegment(sketch, "E58.left", {"start": v(-67.31, 19.05) * mm, "end": v(-67.31, -50.8) * mm, "construction": true});
            skLineSegment(sketch, "E58.right", {"start": v(67.31, 19.05) * mm, "end": v(67.31, -50.8) * mm, "construction": true});
            skPoint(sketch, "E58.middle", {"position": v(0, -15.88) * mm});
            skCircle(sketch, "E59", {"center": v(-67.31, -50.8) * mm, "radius": 2.22 * mm});
            skCircle(sketch, "E60", {"center": v(-67.31, 19.05) * mm, "radius": 2.22 * mm});
            skCircle(sketch, "E61", {"center": v(67.31, 19.05) * mm, "radius": 2.22 * mm});
            skCircle(sketch, "E62", {"center": v(67.31, -50.8) * mm, "radius": 2.22 * mm});
            skSolve(sketch);
        }
        {
            var Q0;
            Q0=qSketchRegion(id+"F39",true);
            extrude(context, id + "F40", {"entities" : qUnion([Q0]), "operationType" : NewBodyOperationType.REMOVE, "oppositeDirection" : true, "depth" : 25.4 * mm});
        }
        {
            var Q0;
            {var subQ0=sQuery(id+"F0.wireOp",EDGE,"E8");var subQ1=sQuery(id+"F0.wireOp",EDGE,"E7");var subQ2=sQuery(id+"F0.wireOp",EDGE,"E6");var subQ3=sQuery(id+"F0.wireOp",EDGE,"E5");var subQ4=sQuery(id+"F0.wireOp",EDGE,"E4.right");var subQ5=sQuery(id+"F0.wireOp",EDGE,"E4.left");var subQ6=sQuery(id+"F0.wireOp",EDGE,"E4.top");var subQ7=sQuery(id+"F0.wireOp",EDGE,"E3");var subQ8=sQuery(id+"F0.wireOp",EDGE,"E2");var subQ9=sQuery(id+"F0.wireOp",EDGE,"E1");var subQ10=sQuery(id+"F0.wireOp",EDGE,"E0");var subQ11=sQuery(id+"F7.wireOp",EDGE,"E15.bottom");Q0=makeQuery(id+"F27.boolean.opBoolean","MERGE",FACE,{"derivedFrom":[makeQuery(id+"F21.boolean.opBoolean","MERGE",FACE,{"derivedFrom":[makeQuery(id+"F8.boolean.opBoolean","MERGE",FACE,{"derivedFrom":[makeQuery(id+"F1.opExtrude","CAP_FACE",FACE,{"disambiguationData":[OSD([subQ10,subQ9,subQ8,subQ7,subQ6,subQ5,subQ4,subQ3,subQ2,subQ1,subQ0])],"isStart":false}),makeQuery(id+"F8.opExtrude","CAP_FACE",FACE,{"disambiguationData":[OSD([subQ10,subQ9,subQ8,subQ7,subQ6,subQ5,subQ4,subQ3,subQ2,subQ1,subQ0]),ownerDisambiguation([makeQuery(id+"F7.imprint","IMPRINT",EDGE,{"disambiguationData":[TD([[makeQuery(id+"F7.imprint","IMPRINT",VERTEX,{"derivedFrom":subQ11}),1.0]])],"derivedFrom":subQ11})])],"isStart":false}),makeQuery(id+"F8.opExtrude","CAP_FACE",FACE,{"disambiguationData":[OSD([subQ10,subQ9,subQ8,subQ7,subQ6,subQ5,subQ4,subQ3,subQ2,subQ1,subQ0]),ownerDisambiguation([makeQuery(id+"F7.imprint","IMPRINT",EDGE,{"derivedFrom":sQuery(id+"F7.wireOp",EDGE,"E17.bottom")})])],"isStart":false})]}),makeQuery(id+"F21.opExtrude","CAP_FACE",FACE,{"disambiguationData":[OSD([sQuery(id+"F20.wireOp",EDGE,"E40"),sQuery(id+"F20.wireOp",EDGE,"E41.0")])],"isStart":true})]}),makeQuery(id+"F27.opExtrude","CAP_FACE",FACE,{"disambiguationData":[OSD([sQuery(id+"F26.wireOp",EDGE,"E48.bottom"),sQuery(id+"F26.wireOp",EDGE,"E48.top"),sQuery(id+"F26.wireOp",EDGE,"E48.left"),sQuery(id+"F26.wireOp",EDGE,"E48.right")])],"isStart":true}),makeQuery(id+"F27.opExtrude","CAP_FACE",FACE,{"disambiguationData":[OSD([sQuery(id+"F26.wireOp",EDGE,"E49.bottom"),sQuery(id+"F26.wireOp",EDGE,"E49.top"),sQuery(id+"F26.wireOp",EDGE,"E49.left"),sQuery(id+"F26.wireOp",EDGE,"E49.right")])],"isStart":true})]});}
            var sketch = newSketch(context, id + "F41", { "sketchPlane" : qUnion([Q0])});
            skCircle(sketch, "E63", {"center": v(-53.98, 47.63) * mm, "radius": 6.35 * mm});
            skSolve(sketch);
        }
        {
            var Q0;
            Q0=qSketchRegion(id+"F41",true);
            extrude(context, id + "F42", {"entities" : qUnion([Q0]), "operationType" : NewBodyOperationType.REMOVE, "oppositeDirection" : true, "depth" : 25.4 * mm});
        }
        {
            var Q0;
            Q0=makeQuery(id+"F36.boolean.opBoolean","MERGE",FACE,{"derivedFrom":[makeQuery(id+"F31.boolean.opBoolean","MERGE",FACE,{"derivedFrom":[makeQuery(id+"F27.boolean.opBoolean","MERGE",FACE,{"derivedFrom":[makeQuery(id+"F25.boolean.opBoolean","COPY",FACE,{"derivedFrom":makeQuery(id+"F25.opExtrude","SWEPT_FACE",FACE,{"disambiguationData":[OSD([sQuery(id+"F24.wireOp",EDGE,"E45.left")])]})}),makeQuery(id+"F27.opExtrude","SWEPT_FACE",FACE,{"disambiguationData":[OSD([sQuery(id+"F26.wireOp",EDGE,"E49.right")])]})]}),makeQuery(id+"F31.opExtrude","CAP_FACE",FACE,{"disambiguationData":[OSD([sQuery(id+"F30.wireOp",EDGE,"E52"),sQuery(id+"F30.wireOp",EDGE,"E53.0")])],"isStart":true})]}),makeQuery(id+"F36.opExtrude","CAP_FACE",FACE,{"disambiguationData":[OSD([sQuery(id+"F35.wireOp",EDGE,"E56")])],"isStart":true})]});
            extrude(context, id + "F43", {"entities" : qUnion([Q0]), "operationType" : NewBodyOperationType.REMOVE, "oppositeDirection" : true, "depth" : 1.27 * mm});
        }
        {
            var Q0;
            Q0=makeQuery(id+"F38.boolean.opBoolean","MERGE",FACE,{"derivedFrom":[makeQuery(id+"F33.boolean.opBoolean","MERGE",FACE,{"derivedFrom":[makeQuery(id+"F27.boolean.opBoolean","MERGE",FACE,{"derivedFrom":[makeQuery(id+"F25.boolean.opBoolean","COPY",FACE,{"derivedFrom":makeQuery(id+"F25.opExtrude","SWEPT_FACE",FACE,{"disambiguationData":[OSD([sQuery(id+"F24.wireOp",EDGE,"E44.left")])]})}),makeQuery(id+"F27.opExtrude","SWEPT_FACE",FACE,{"disambiguationData":[OSD([sQuery(id+"F26.wireOp",EDGE,"E48.right")])]})]}),makeQuery(id+"F33.opExtrude","CAP_FACE",FACE,{"disambiguationData":[OSD([sQuery(id+"F32.wireOp",EDGE,"E54"),sQuery(id+"F32.wireOp",EDGE,"E55.0")])],"isStart":true})]}),makeQuery(id+"F38.opExtrude","CAP_FACE",FACE,{"disambiguationData":[OSD([sQuery(id+"F37.wireOp",EDGE,"E57.0"),sQuery(id+"F37.wireOp",EDGE,"E57.1"),sQuery(id+"F37.wireOp",EDGE,"E57.2"),sQuery(id+"F37.wireOp",EDGE,"E57.3"),sQuery(id+"F37.wireOp",EDGE,"E57.4"),sQuery(id+"F37.wireOp",EDGE,"E57.5")])],"isStart":true})]});
            extrude(context, id + "F44", {"entities" : qUnion([Q0]), "operationType" : NewBodyOperationType.REMOVE, "oppositeDirection" : true, "depth" : 1.27 * mm});
        }
        {
            var Q0;
            Q0=makeQuery(id+"F43.boolean.opBoolean","COPY",FACE,{"derivedFrom":makeQuery(id+"F43.opExtrude","CAP_FACE",FACE,{"disambiguationData":[OSD([sQuery(id+"F24.wireOp",EDGE,"E45.left"),sQuery(id+"F26.wireOp",EDGE,"E49.right"),sQuery(id+"F30.wireOp",EDGE,"E52"),sQuery(id+"F30.wireOp",EDGE,"E53.0"),sQuery(id+"F35.wireOp",EDGE,"E56")])],"isStart":false})});
            var sketch = newSketch(context, id + "F45", { "sketchPlane" : qUnion([Q0])});
            skLineSegment(sketch, "E64.0", {"start": v(0, 114.3) * mm, "end": v(-3.27, 114.3) * mm});
            skLineSegment(sketch, "E64.1", {"start": v(0, 123.37) * mm, "end": v(0, 114.3) * mm});
            skLineSegment(sketch, "E64.2", {"start": v(-12.7, 123.37) * mm, "end": v(-12.7, 114.3) * mm});
            skLineSegment(sketch, "E64.3", {"start": v(-9.43, 114.3) * mm, "end": v(-12.7, 114.3) * mm});
            skArc(sketch, "E64.4", {"start": v(0, 123.37) * mm, "mid": v(-6.35, 126.68) * mm, "end": v(-12.7, 123.37) * mm});
            skArc(sketch, "E65", {"start": v(-3.27, 114.3) * mm, "mid": v(-6.35, 124.48) * mm, "end": v(-9.43, 114.3) * mm});
            skSolve(sketch);
        }
        {
            var Q0;
            Q0=qSketchRegion(id+"F45",true);
            extrude(context, id + "F46", {"entities" : qUnion([Q0]), "operationType" : NewBodyOperationType.ADD, "depth" : 6.35 * mm});
        }
        {
            var Q0;
            Q0=makeQuery(id+"F44.boolean.opBoolean","COPY",FACE,{"derivedFrom":makeQuery(id+"F44.opExtrude","CAP_FACE",FACE,{"disambiguationData":[OSD([sQuery(id+"F24.wireOp",EDGE,"E44.left"),sQuery(id+"F26.wireOp",EDGE,"E48.right"),sQuery(id+"F32.wireOp",EDGE,"E54"),sQuery(id+"F32.wireOp",EDGE,"E55.0"),sQuery(id+"F37.wireOp",EDGE,"E57.0"),sQuery(id+"F37.wireOp",EDGE,"E57.1"),sQuery(id+"F37.wireOp",EDGE,"E57.2"),sQuery(id+"F37.wireOp",EDGE,"E57.3"),sQuery(id+"F37.wireOp",EDGE,"E57.4"),sQuery(id+"F37.wireOp",EDGE,"E57.5")])],"isStart":false})});
            var sketch = newSketch(context, id + "F47", { "sketchPlane" : qUnion([Q0])});
            skCircle(sketch, "E66.cCircle", {"center": v(6.35, 118.93) * mm, "radius": 6.6 * mm, "construction": true});
            skLineSegment(sketch, "E66.0", {"start": v(2.93, 114.3) * mm, "end": v(0.63, 115.63) * mm});
            skLineSegment(sketch, "E66.1", {"start": v(0.63, 115.63) * mm, "end": v(0.63, 122.23) * mm});
            skLineSegment(sketch, "E66.2", {"start": v(0.63, 122.23) * mm, "end": v(6.35, 125.53) * mm});
            skLineSegment(sketch, "E66.3", {"start": v(6.35, 125.53) * mm, "end": v(12.07, 122.23) * mm});
            skLineSegment(sketch, "E66.4", {"start": v(12.07, 122.23) * mm, "end": v(12.07, 115.63) * mm});
            skLineSegment(sketch, "E66.5", {"start": v(12.07, 115.63) * mm, "end": v(9.77, 114.3) * mm});
            skArc(sketch, "E67.0", {"start": v(12.7, 123.37) * mm, "mid": v(6.35, 126.68) * mm, "end": v(0, 123.37) * mm});
            skLineSegment(sketch, "E68.0", {"start": v(12.7, 123.37) * mm, "end": v(12.7, 114.3) * mm});
            skLineSegment(sketch, "E69.0", {"start": v(0, 123.37) * mm, "end": v(0, 114.3) * mm});
            skLineSegment(sketch, "E70.0", {"start": v(9.77, 114.3) * mm, "end": v(12.7, 114.3) * mm});
            skLineSegment(sketch, "E71.0", {"start": v(0, 114.3) * mm, "end": v(2.93, 114.3) * mm});
            skPoint(sketch, "E72.orphan", {"position": v(6.35, 112.32) * mm});
            skSolve(sketch);
        }
        {
            var Q0;
            Q0=qSketchRegion(id+"F47",true);
            extrude(context, id + "F48", {"entities" : qUnion([Q0]), "operationType" : NewBodyOperationType.ADD, "depth" : 6.35 * mm});
        }
        {
            var Q0;
            {var subQ0=sQuery(id+"F0.wireOp",EDGE,"E8");var subQ1=sQuery(id+"F0.wireOp",EDGE,"E7");var subQ2=sQuery(id+"F0.wireOp",EDGE,"E6");var subQ3=sQuery(id+"F0.wireOp",EDGE,"E5");var subQ4=sQuery(id+"F0.wireOp",EDGE,"E4.right");var subQ5=sQuery(id+"F0.wireOp",EDGE,"E4.left");var subQ6=sQuery(id+"F0.wireOp",EDGE,"E4.top");var subQ7=sQuery(id+"F0.wireOp",EDGE,"E3");var subQ8=sQuery(id+"F0.wireOp",EDGE,"E2");var subQ9=sQuery(id+"F0.wireOp",EDGE,"E1");var subQ10=sQuery(id+"F0.wireOp",EDGE,"E0");var subQ11=sQuery(id+"F7.wireOp",EDGE,"E15.bottom");Q0=makeQuery(id+"F48.boolean.opBoolean","MERGE",FACE,{"derivedFrom":[makeQuery(id+"F46.boolean.opBoolean","MERGE",FACE,{"derivedFrom":[makeQuery(id+"F27.boolean.opBoolean","MERGE",FACE,{"derivedFrom":[makeQuery(id+"F21.boolean.opBoolean","MERGE",FACE,{"derivedFrom":[makeQuery(id+"F8.boolean.opBoolean","MERGE",FACE,{"derivedFrom":[makeQuery(id+"F1.opExtrude","CAP_FACE",FACE,{"disambiguationData":[OSD([subQ10,subQ9,subQ8,subQ7,subQ6,subQ5,subQ4,subQ3,subQ2,subQ1,subQ0])],"isStart":false}),makeQuery(id+"F8.opExtrude","CAP_FACE",FACE,{"disambiguationData":[OSD([subQ10,subQ9,subQ8,subQ7,subQ6,subQ5,subQ4,subQ3,subQ2,subQ1,subQ0]),ownerDisambiguation([makeQuery(id+"F7.imprint","IMPRINT",EDGE,{"disambiguationData":[TD([[makeQuery(id+"F7.imprint","IMPRINT",VERTEX,{"derivedFrom":subQ11}),1.0]])],"derivedFrom":subQ11})])],"isStart":false}),makeQuery(id+"F8.opExtrude","CAP_FACE",FACE,{"disambiguationData":[OSD([subQ10,subQ9,subQ8,subQ7,subQ6,subQ5,subQ4,subQ3,subQ2,subQ1,subQ0]),ownerDisambiguation([makeQuery(id+"F7.imprint","IMPRINT",EDGE,{"derivedFrom":sQuery(id+"F7.wireOp",EDGE,"E17.bottom")})])],"isStart":false})]}),makeQuery(id+"F21.opExtrude","CAP_FACE",FACE,{"disambiguationData":[OSD([sQuery(id+"F20.wireOp",EDGE,"E40"),sQuery(id+"F20.wireOp",EDGE,"E41.0")])],"isStart":true})]}),makeQuery(id+"F27.opExtrude","CAP_FACE",FACE,{"disambiguationData":[OSD([sQuery(id+"F26.wireOp",EDGE,"E48.bottom"),sQuery(id+"F26.wireOp",EDGE,"E48.top"),sQuery(id+"F26.wireOp",EDGE,"E48.left"),sQuery(id+"F26.wireOp",EDGE,"E48.right")])],"isStart":true}),makeQuery(id+"F27.opExtrude","CAP_FACE",FACE,{"disambiguationData":[OSD([sQuery(id+"F26.wireOp",EDGE,"E49.bottom"),sQuery(id+"F26.wireOp",EDGE,"E49.top"),sQuery(id+"F26.wireOp",EDGE,"E49.left"),sQuery(id+"F26.wireOp",EDGE,"E49.right")])],"isStart":true})]}),makeQuery(id+"F46.opExtrude","SWEPT_FACE",FACE,{"disambiguationData":[OSD([sQuery(id+"F45.wireOp",EDGE,"E64.2")])]})]}),makeQuery(id+"F48.opExtrude","SWEPT_FACE",FACE,{"disambiguationData":[OSD([sQuery(id+"F47.wireOp",EDGE,"E68.0")])]})]});}
            var sketch = newSketch(context, id + "F49", { "sketchPlane" : qUnion([Q0])});
            skLineSegment(sketch, "E73.bottom", {"start": v(-50.01, -63.5) * mm, "end": v(50.01, -63.5) * mm});
            skLineSegment(sketch, "E73.top", {"start": v(-50.01, -41.33) * mm, "end": v(50.01, -41.33) * mm});
            skLineSegment(sketch, "E73.left", {"start": v(-50.01, -63.5) * mm, "end": v(-50.01, -41.33) * mm});
            skLineSegment(sketch, "E73.right", {"start": v(50.01, -63.5) * mm, "end": v(50.01, -41.33) * mm});
            skPoint(sketch, "E73.middle", {"position": v(0, -52.41) * mm});
            skSolve(sketch);
        }
        {
            var Q0;
            Q0=qSketchRegion(id+"F49",true);
            extrude(context, id + "F50", {"entities" : qUnion([Q0]), "operationType" : NewBodyOperationType.ADD, "oppositeDirection" : true, "depth" : 12.7 * mm});
        }
        {
            var Q0;
            Q0=makeQuery(id+"F50.boolean.opBoolean","INTERSECT",EDGE,{"disambiguationData":[OD(0.0)],"derivedFrom":[makeQuery(id+"F3.boolean.opBoolean","COPY",FACE,{"derivedFrom":makeQuery(id+"F3.opExtrude","SWEPT_FACE",FACE,{"disambiguationData":[OSD([sQuery(id+"F2.wireOp",EDGE,"E10")])]})}),makeQuery(id+"F50.opExtrude","SWEPT_FACE",FACE,{"disambiguationData":[OSD([sQuery(id+"F49.wireOp",EDGE,"E73.bottom")])]})]});
            var Q1;
            Q1=makeQuery(id+"F50.boolean.opBoolean","INTERSECT",EDGE,{"disambiguationData":[OD(1.0)],"derivedFrom":[makeQuery(id+"F3.boolean.opBoolean","COPY",FACE,{"derivedFrom":makeQuery(id+"F3.opExtrude","SWEPT_FACE",FACE,{"disambiguationData":[OSD([sQuery(id+"F2.wireOp",EDGE,"E10")])]})}),makeQuery(id+"F50.opExtrude","SWEPT_FACE",FACE,{"disambiguationData":[OSD([sQuery(id+"F49.wireOp",EDGE,"E73.bottom")])]})]});
            fillet(context, id + "F51", {"entities" : qUnion([Q0, Q1]), "radius" : 5.08 * mm, "tangentPropagation" : true, "allowEdgeOverflow" : false});
        }
    });
